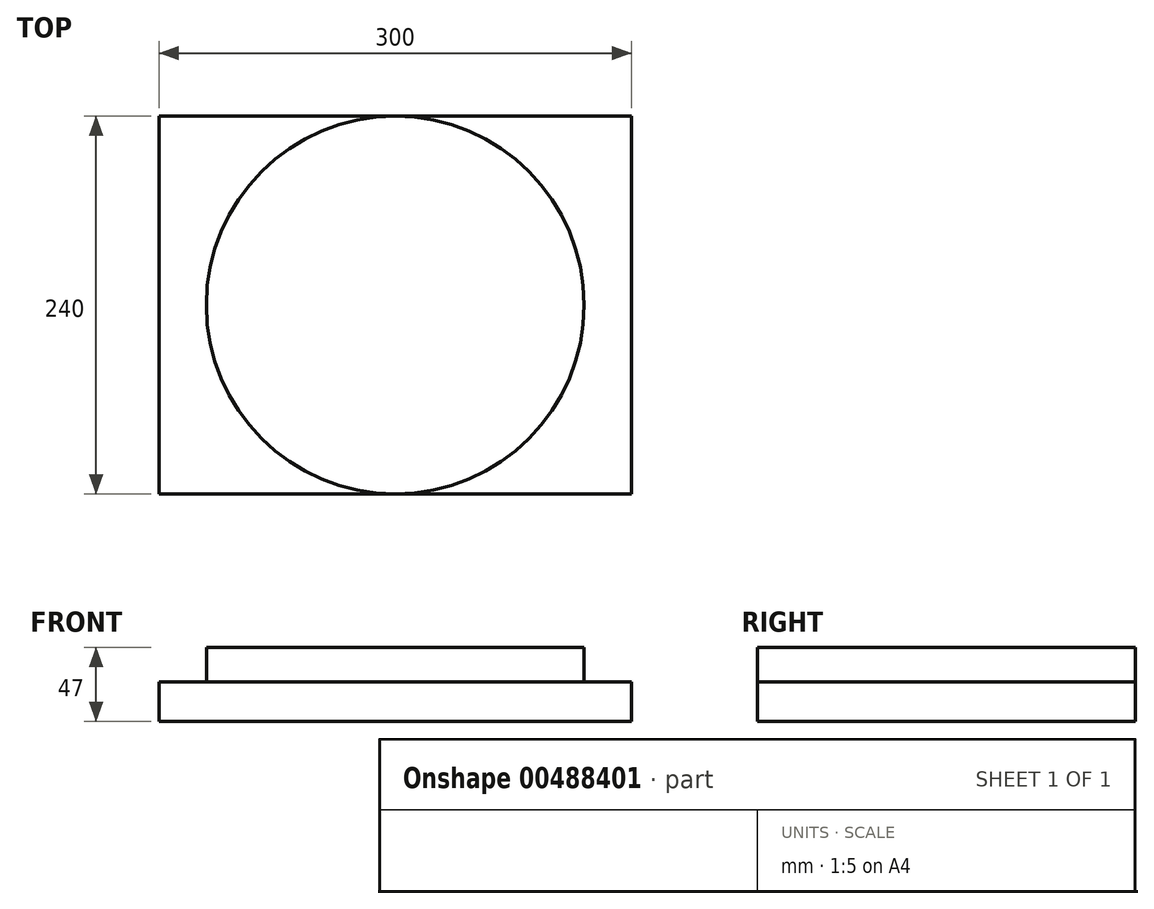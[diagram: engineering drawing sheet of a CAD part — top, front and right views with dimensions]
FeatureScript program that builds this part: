
annotation { "Feature Type Name" : "Feature", "Feature Type Description" : "" }
export const myFeature = defineFeature(function(context is Context, id is Id, definition is map)
    precondition{}
    {
        {
            var Q0;
            Q0=qCreatedBy(makeId("Top.planeOp"),FACE);
            var sketch = newSketch(context, id + "F0", { "sketchPlane" : qUnion([Q0])});
            skCircle(sketch, "E0", {"center": v(0, 0) * mm, "radius": 120 * mm});
            skCircle(sketch, "E1", {"center": v(0, 0) * mm, "radius": 100 * mm});
            skSolve(sketch);
        }
        {
            var Q0;
            Q0=makeQuery(id+"F0.imprint","IMPRINT",FACE,{"disambiguationData":[TD([[makeQuery(id+"F0.imprint","IMPRINT",EDGE,{"derivedFrom":sQuery(id+"F0.wireOp",EDGE,"E0")}),1.0]])]});
            var Q1;
            Q1=makeQuery(id+"F0.imprint","IMPRINT",FACE,{"disambiguationData":[TD([[makeQuery(id+"F0.imprint","IMPRINT",EDGE,{"derivedFrom":sQuery(id+"F0.wireOp",EDGE,"E1")}),1.0]])]});
            extrude(context, id + "F1", {"entities" : qUnion([Q0, Q1]), "oppositeDirection" : true, "depth" : 9 * mm});
        }
        {
            var Q0;
            Q0=makeQuery(id+"F0.imprint","IMPRINT",FACE,{"disambiguationData":[TD([[makeQuery(id+"F0.imprint","IMPRINT",EDGE,{"derivedFrom":sQuery(id+"F0.wireOp",EDGE,"E1")}),1.0]])]});
            extrude(context, id + "F2", {"entities" : qUnion([Q0]), "depth" : 4 * mm});
        }
        {
            var Q0;
            Q0=makeQuery(id+"F0.imprint","IMPRINT",FACE,{"disambiguationData":[TD([[makeQuery(id+"F0.imprint","IMPRINT",EDGE,{"derivedFrom":sQuery(id+"F0.wireOp",EDGE,"E0")}),1.0]])]});
            extrude(context, id + "F3", {"entities" : qUnion([Q0]), "operationType" : NewBodyOperationType.ADD, "depth" : 13 * mm});
        }
        {
            var Q0;
            Q0=makeQuery(id+"F2.opExtrude","CAP_FACE",FACE,{"disambiguationData":[OSD([sQuery(id+"F0.wireOp",EDGE,"E1")])],"isStart":false});
            extrude(context, id + "F4", {"entities" : qUnion([Q0]), "operationType" : NewBodyOperationType.ADD, "depth" : 9 * mm});
        }
        {
            var Q0;
            Q0=makeQuery(id+"F1.opExtrude","CAP_FACE",FACE,{"disambiguationData":[OSD([sQuery(id+"F0.wireOp",EDGE,"E0")])],"isStart":false});
            var sketch = newSketch(context, id + "F5", { "sketchPlane" : qUnion([Q0])});
            skLineSegment(sketch, "E2.bottom", {"start": v(150, 120) * mm, "end": v(-150, 120) * mm});
            skLineSegment(sketch, "E2.top", {"start": v(150, -120) * mm, "end": v(-150, -120) * mm});
            skLineSegment(sketch, "E2.left", {"start": v(150, 120) * mm, "end": v(150, -120) * mm});
            skLineSegment(sketch, "E2.right", {"start": v(-150, 120) * mm, "end": v(-150, -120) * mm});
            skPoint(sketch, "E2.middle", {"position": v(0, 0) * mm});
            skSolve(sketch);
        }
        {
            var Q0;
            {var subQ0=makeQuery(id+"F1.opExtrude","CAP_EDGE",EDGE,{"disambiguationData":[OSD([sQuery(id+"F0.wireOp",EDGE,"E0")])],"isStart":false});var subQ1=makeQuery(id+"F5.imprint","INTERSECT",VERTEX,{"derivedFrom":[subQ0,sQuery(id+"F5.wireOp",EDGE,"E2.bottom")]});Q0=makeQuery(id+"F5.imprint","IMPRINT",FACE,{"disambiguationData":[TD([[makeQuery(id+"F5.imprint","IMPRINT",EDGE,{"disambiguationData":[TD([[subQ1,-1.0]])],"derivedFrom":subQ0}),-1.0]])]});}
            var Q1;
            {var subQ0=sQuery(id+"F5.wireOp",EDGE,"E2.left");var subQ1=sQuery(id+"F5.wireOp",EDGE,"E2.bottom");var subQ2=makeQuery(id+"F5.imprint","INTERSECT",VERTEX,{"derivedFrom":[subQ1,subQ0]});Q1=makeQuery(id+"F5.imprint","IMPRINT",FACE,{"disambiguationData":[TD([[makeQuery(id+"F5.imprint","IMPRINT",EDGE,{"disambiguationData":[TD([[subQ2,-1.0]])],"derivedFrom":subQ1}),1.0]])]});}
            var Q2;
            {var subQ0=sQuery(id+"F5.wireOp",EDGE,"E2.right");var subQ1=sQuery(id+"F5.wireOp",EDGE,"E2.bottom");var subQ2=makeQuery(id+"F5.imprint","INTERSECT",VERTEX,{"derivedFrom":[subQ1,subQ0]});Q2=makeQuery(id+"F5.imprint","IMPRINT",FACE,{"disambiguationData":[TD([[makeQuery(id+"F5.imprint","IMPRINT",EDGE,{"disambiguationData":[TD([[subQ2,1.0]])],"derivedFrom":subQ1}),1.0]])]});}
            var Q3;
            {var subQ0=sQuery(id+"F5.wireOp",EDGE,"E2.right");var subQ1=sQuery(id+"F5.wireOp",EDGE,"E2.top");var subQ2=makeQuery(id+"F5.imprint","INTERSECT",VERTEX,{"derivedFrom":[subQ1,subQ0]});Q3=makeQuery(id+"F5.imprint","IMPRINT",FACE,{"disambiguationData":[TD([[makeQuery(id+"F5.imprint","IMPRINT",EDGE,{"disambiguationData":[TD([[subQ2,1.0]])],"derivedFrom":subQ1}),-1.0]])]});}
            var Q4;
            {var subQ0=sQuery(id+"F5.wireOp",EDGE,"E2.left");var subQ1=sQuery(id+"F5.wireOp",EDGE,"E2.top");var subQ2=makeQuery(id+"F5.imprint","INTERSECT",VERTEX,{"derivedFrom":[subQ1,subQ0]});Q4=makeQuery(id+"F5.imprint","IMPRINT",FACE,{"disambiguationData":[TD([[makeQuery(id+"F5.imprint","IMPRINT",EDGE,{"disambiguationData":[TD([[subQ2,-1.0]])],"derivedFrom":subQ1}),-1.0]])]});}
            extrude(context, id + "F6", {"entities" : qUnion([Q0, Q1, Q2, Q3, Q4]), "depth" : 25 * mm});
        }
    });
